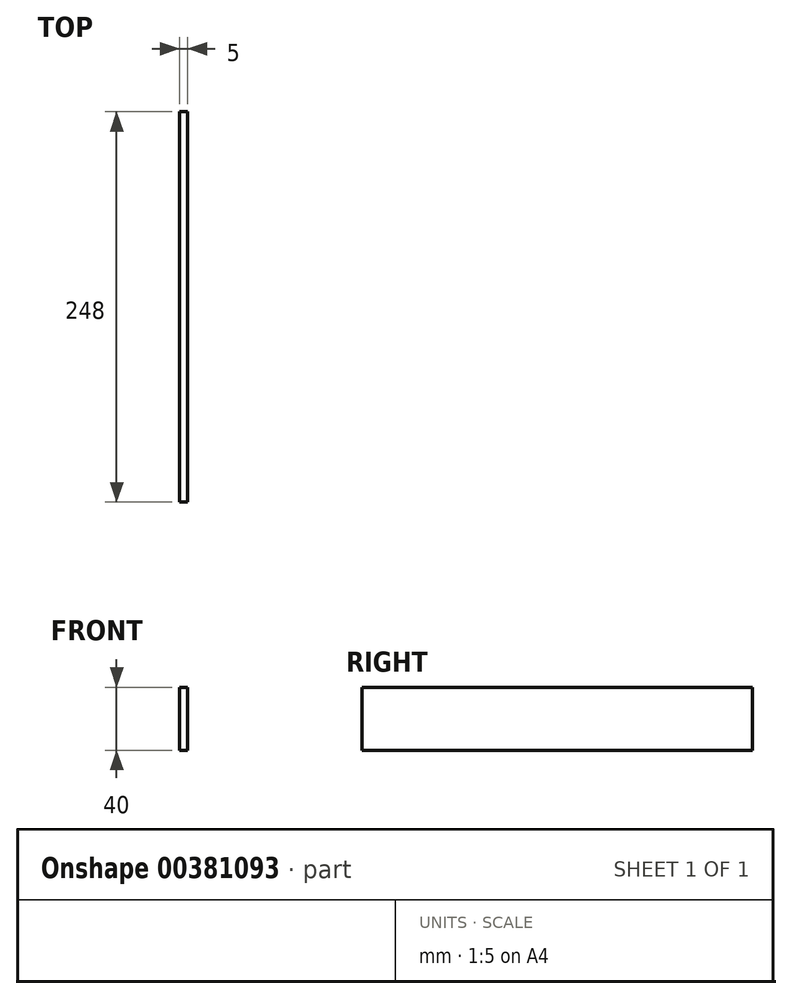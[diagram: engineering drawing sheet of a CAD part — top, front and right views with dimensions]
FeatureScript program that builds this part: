
annotation { "Feature Type Name" : "Feature", "Feature Type Description" : "" }
export const myFeature = defineFeature(function(context is Context, id is Id, definition is map)
    precondition{}
    {
        {
            var Q0;
            Q0=qCreatedBy(makeId("Top.planeOp"),FACE);
            var sketch = newSketch(context, id + "F0", { "sketchPlane" : qUnion([Q0])});
            skLineSegment(sketch, "E0.bottom", {"start": v(-2.5, 124) * mm, "end": v(2.5, 124) * mm});
            skLineSegment(sketch, "E0.top", {"start": v(-2.5, -124) * mm, "end": v(2.5, -124) * mm});
            skLineSegment(sketch, "E0.left", {"start": v(-2.5, 124) * mm, "end": v(-2.5, -124) * mm});
            skLineSegment(sketch, "E0.right", {"start": v(2.5, 124) * mm, "end": v(2.5, -124) * mm});
            skSolve(sketch);
        }
        {
            var Q0;
            Q0=makeQuery(id+"F0.imprint","IMPRINT",FACE,{"disambiguationData":[TD([[makeQuery(id+"F0.imprint","IMPRINT",EDGE,{"derivedFrom":sQuery(id+"F0.wireOp",EDGE,"E0.bottom")}),-1.0]])]});
            extrude(context, id + "F1", {"entities" : qUnion([Q0]), "depth" : 40 * mm});
        }
    });
